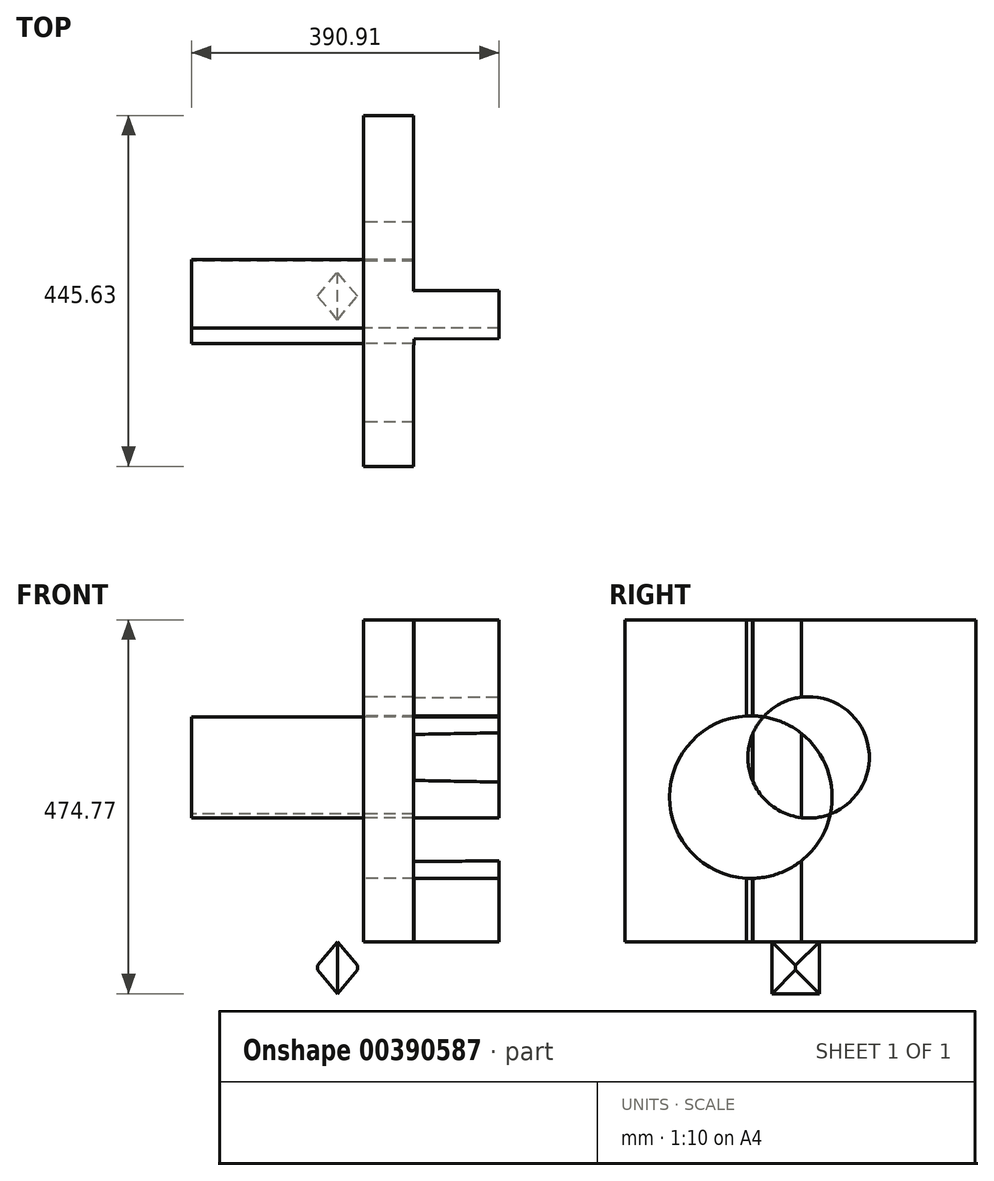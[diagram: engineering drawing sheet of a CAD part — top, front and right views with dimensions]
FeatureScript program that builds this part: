
annotation { "Feature Type Name" : "Feature", "Feature Type Description" : "" }
export const myFeature = defineFeature(function(context is Context, id is Id, definition is map)
    precondition{}
    {
        {
            var Q0;
            Q0=qCreatedBy(makeId("Front.planeOp"),FACE);
            var sketch = newSketch(context, id + "F0", { "sketchPlane" : qUnion([Q0])});
            skSolve(sketch);
        }
        {
            var Q0;
            Q0=qCreatedBy(makeId("Right.planeOp"),FACE);
            var sketch = newSketch(context, id + "F1", { "sketchPlane" : qUnion([Q0])});
            skLineSegment(sketch, "E0.bottom", {"start": v(11.62, 0) * mm, "end": v(71.87, 0) * mm});
            skLineSegment(sketch, "E0.top", {"start": v(11.62, -65.94) * mm, "end": v(71.87, -65.94) * mm});
            skLineSegment(sketch, "E0.left", {"start": v(11.62, 0) * mm, "end": v(11.62, -65.94) * mm});
            skLineSegment(sketch, "E0.right", {"start": v(71.87, 0) * mm, "end": v(71.87, -65.94) * mm});
            skSolve(sketch);
        }
        {
            var Q0;
            Q0=makeQuery(id+"F1.imprint","IMPRINT",FACE,{"disambiguationData":[TD([[makeQuery(id+"F1.imprint","IMPRINT",EDGE,{"derivedFrom":sQuery(id+"F1.wireOp",EDGE,"E0.bottom")}),-1.0]])]});
            extrude(context, id + "F2", {"entities" : qUnion([Q0]), "endBound" : BoundingType.SYMMETRIC, "depth" : 127 * mm, "hasDraft" : true, "draftAngle" : 50 * degree, "draftPullDirection" : true});
        }
        {
            var Q0;
            Q0=qCreatedBy(makeId("Top.planeOp"),FACE);
            var sketch = newSketch(context, id + "F3", { "sketchPlane" : qUnion([Q0])});
            skArc(sketch, "E1", {"start": v(33.02, -16.8) * mm, "mid": v(67.07, -47.06) * mm, "end": v(97.34, -13.01) * mm});
            skLineSegment(sketch, "E2", {"start": v(33.02, 48.16) * mm, "end": v(33.02, -16.8) * mm});
            skLineSegment(sketch, "E3", {"start": v(96.84, 48.16) * mm, "end": v(33.02, 48.16) * mm});
            skLineSegment(sketch, "E4", {"start": v(96.84, 48.16) * mm, "end": v(97.34, -13.01) * mm});
            skSolve(sketch);
        }
        {
            var Q0;
            Q0=makeQuery(id+"F3.imprint","IMPRINT",FACE,{"disambiguationData":[TD([[makeQuery(id+"F3.imprint","IMPRINT",EDGE,{"derivedFrom":sQuery(id+"F3.wireOp",EDGE,"E1")}),1.0]])]});
            var sketch = newSketch(context, id + "F4", { "sketchPlane" : qUnion([Q0])});
            skSolve(sketch);
        }
        {
            var Q0;
            Q0=makeQuery(id+"F4.imprint","IMPRINT",FACE,{"disambiguationData":[TD([[makeQuery(id+"F4.imprint","IMPRINT",EDGE,{"derivedFrom":makeQuery(id+"F3.imprint","IMPRINT",EDGE,{"derivedFrom":sQuery(id+"F3.wireOp",EDGE,"E1")})}),1.0]])]});
            extrude(context, id + "F5", {"entities" : qUnion([Q0]), "depth" : 408.83 * mm});
        }
        {
            var Q0;
            Q0=makeQuery(id+"F5.opExtrude","CAP_FACE",FACE,{"disambiguationData":[OSD([sQuery(id+"F3.wireOp",EDGE,"E1"),sQuery(id+"F3.wireOp",EDGE,"E2"),sQuery(id+"F3.wireOp",EDGE,"E3"),sQuery(id+"F3.wireOp",EDGE,"E4")])],"isStart":false});
            var sketch = newSketch(context, id + "F6", { "sketchPlane" : qUnion([Q0])});
            skSolve(sketch);
        }
        {
            var Q0;
            Q0=makeQuery(id+"F5.opExtrude","SWEPT_FACE",FACE,{"disambiguationData":[OSD([sQuery(id+"F3.wireOp",EDGE,"E3")])]});
            extrude(context, id + "F7", {"entities" : qUnion([Q0]), "operationType" : NewBodyOperationType.ADD, "endBound" : BoundingType.SYMMETRIC, "depth" : 445.62 * mm});
        }
        {
            var Q0;
            Q0=makeQuery(id+"F5.opExtrude","SWEPT_FACE",FACE,{"disambiguationData":[OSD([sQuery(id+"F3.wireOp",EDGE,"E4")])]});
            var sketch = newSketch(context, id + "F8", { "sketchPlane" : qUnion([Q0])});
            skSolve(sketch);
        }
        {
            var Q0;
            {var subQ0=sQuery(id+"F3.wireOp",EDGE,"E4");Q0=makeQuery(id+"F8.imprint","IMPRINT",FACE,{"disambiguationData":[TD([[makeQuery(id+"F8.imprint","IMPRINT",EDGE,{"derivedFrom":makeQuery(id+"F5.opExtrude","CAP_EDGE",EDGE,{"disambiguationData":[OSD([subQ0])],"isStart":true})}),-1.0]])]});}
            extrude(context, id + "F9", {"entities" : qUnion([Q0]), "operationType" : NewBodyOperationType.ADD, "depth" : 108.13 * mm});
        }
        {
            var Q0;
            {var subQ0=sQuery(id+"F3.wireOp",EDGE,"E2");Q0=makeQuery(id+"F7.boolean.opBoolean","MERGE",FACE,{"derivedFrom":[makeQuery(id+"F5.opExtrude","SWEPT_FACE",FACE,{"disambiguationData":[OSD([subQ0])]}),makeQuery(id+"F7.opExtrude","SWEPT_FACE",FACE,{"disambiguationData":[OSD([subQ0,sQuery(id+"F3.wireOp",EDGE,"E3")])]})]});}
            var sketch = newSketch(context, id + "F10", { "sketchPlane" : qUnion([Q0])});
            skCircle(sketch, "E5", {"center": v(14.94, 183.75) * mm, "radius": 103.26 * mm});
            skPoint(sketch, "E5.first.point", {"position": v(-83.52, 214.86) * mm});
            skPoint(sketch, "E5.second.point", {"position": v(86.55, 258.15) * mm});
            skPoint(sketch, "E5.third.point", {"position": v(-87.74, 194.71) * mm});
            skCircle(sketch, "E6", {"center": v(-58.36, 234.17) * mm, "radius": 77.12 * mm});
            skPoint(sketch, "E6.first.point", {"position": v(0, 183.75) * mm});
            skPoint(sketch, "E6.second.point", {"position": v(-133.03, 214.86) * mm});
            skPoint(sketch, "E6.third.point", {"position": v(14.94, 258.15) * mm});
            skSolve(sketch);
        }
        {
            var Q0;
            {var subQ0=sQuery(id+"F10.wireOp",EDGE,"E6");var subQ1=sQuery(id+"F10.wireOp",EDGE,"E5");var subQ2=makeQuery(id+"F10.imprint","INTERSECT",VERTEX,{"disambiguationData":[OD(0.0)],"derivedFrom":[subQ1,subQ0]});Q0=makeQuery(id+"F10.imprint","IMPRINT",FACE,{"disambiguationData":[TD([[makeQuery(id+"F10.imprint","IMPRINT",EDGE,{"disambiguationData":[TD([[subQ2,1.0]])],"derivedFrom":subQ1}),1.0]])]});}
            var Q1;
            {var subQ0=sQuery(id+"F10.wireOp",EDGE,"E6");var subQ1=sQuery(id+"F10.wireOp",EDGE,"E5");var subQ2=makeQuery(id+"F10.imprint","INTERSECT",VERTEX,{"disambiguationData":[OD(0.0)],"derivedFrom":[subQ1,subQ0]});Q1=makeQuery(id+"F10.imprint","IMPRINT",FACE,{"disambiguationData":[TD([[makeQuery(id+"F10.imprint","IMPRINT",EDGE,{"disambiguationData":[TD([[subQ2,-1.0]])],"derivedFrom":subQ1}),-1.0]])]});}
            extrude(context, id + "F11", {"entities" : qUnion([Q0, Q1]), "operationType" : NewBodyOperationType.REMOVE, "oppositeDirection" : true, "depth" : 268.8 * mm, "hasSecondDirection" : true, "secondDirectionOppositeDirection" : false, "secondDirectionDepth" : 304.1 * mm});
        }
        {
            var Q0;
            {var subQ0=sQuery(id+"F10.wireOp",EDGE,"E6");var subQ1=sQuery(id+"F10.wireOp",EDGE,"E5");var subQ2=makeQuery(id+"F10.imprint","INTERSECT",VERTEX,{"disambiguationData":[OD(0.0)],"derivedFrom":[subQ1,subQ0]});var subQ4=sQuery(id+"F3.wireOp",EDGE,"E2");Q0=makeQuery(id+"F11.boolean.opBoolean","SPLIT",FACE,{"disambiguationData":[TD([makeQuery(id+"F11.opExtrude","SWEPT_FACE",FACE,{"disambiguationData":[OSD([subQ1]),TDD([makeQuery(id+"F10.imprint","IMPRINT",EDGE,{"disambiguationData":[TD([[subQ2,-1.0]])],"derivedFrom":subQ1})])]})])],"derivedFrom":makeQuery(id+"F7.boolean.opBoolean","MERGE",FACE,{"derivedFrom":[makeQuery(id+"F5.opExtrude","SWEPT_FACE",FACE,{"disambiguationData":[OSD([subQ4])]}),makeQuery(id+"F7.opExtrude","SWEPT_FACE",FACE,{"disambiguationData":[OSD([subQ4,sQuery(id+"F3.wireOp",EDGE,"E3")])]})]})});}
            var Q1;
            {var subQ0=sQuery(id+"F3.wireOp",EDGE,"E4");var subQ1=sQuery(id+"F3.wireOp",EDGE,"E1");var subQ2=sQuery(id+"F3.wireOp",EDGE,"E3");var subQ3=sQuery(id+"F10.wireOp",EDGE,"E6");var subQ4=sQuery(id+"F10.wireOp",EDGE,"E5");var subQ5=makeQuery(id+"F10.imprint","INTERSECT",VERTEX,{"disambiguationData":[OD(0.0)],"derivedFrom":[subQ4,subQ3]});Q1=makeQuery(id+"F11.boolean.opBoolean","SPLIT",FACE,{"disambiguationData":[TD([makeQuery(id+"F11.opExtrude","SWEPT_FACE",FACE,{"disambiguationData":[OSD([subQ4]),TDD([makeQuery(id+"F10.imprint","IMPRINT",EDGE,{"disambiguationData":[TD([[subQ5,-1.0]])],"derivedFrom":subQ4})])]})])],"derivedFrom":makeQuery(id+"F9.opExtrude","CAP_FACE",FACE,{"disambiguationData":[OSD([subQ1,subQ2,subQ0])],"isStart":false})});}
            extrude(context, id + "F12", {"entities" : qUnion([Q0, Q1]), "operationType" : NewBodyOperationType.ADD, "depth" : 218.47 * mm});
        }
    });
